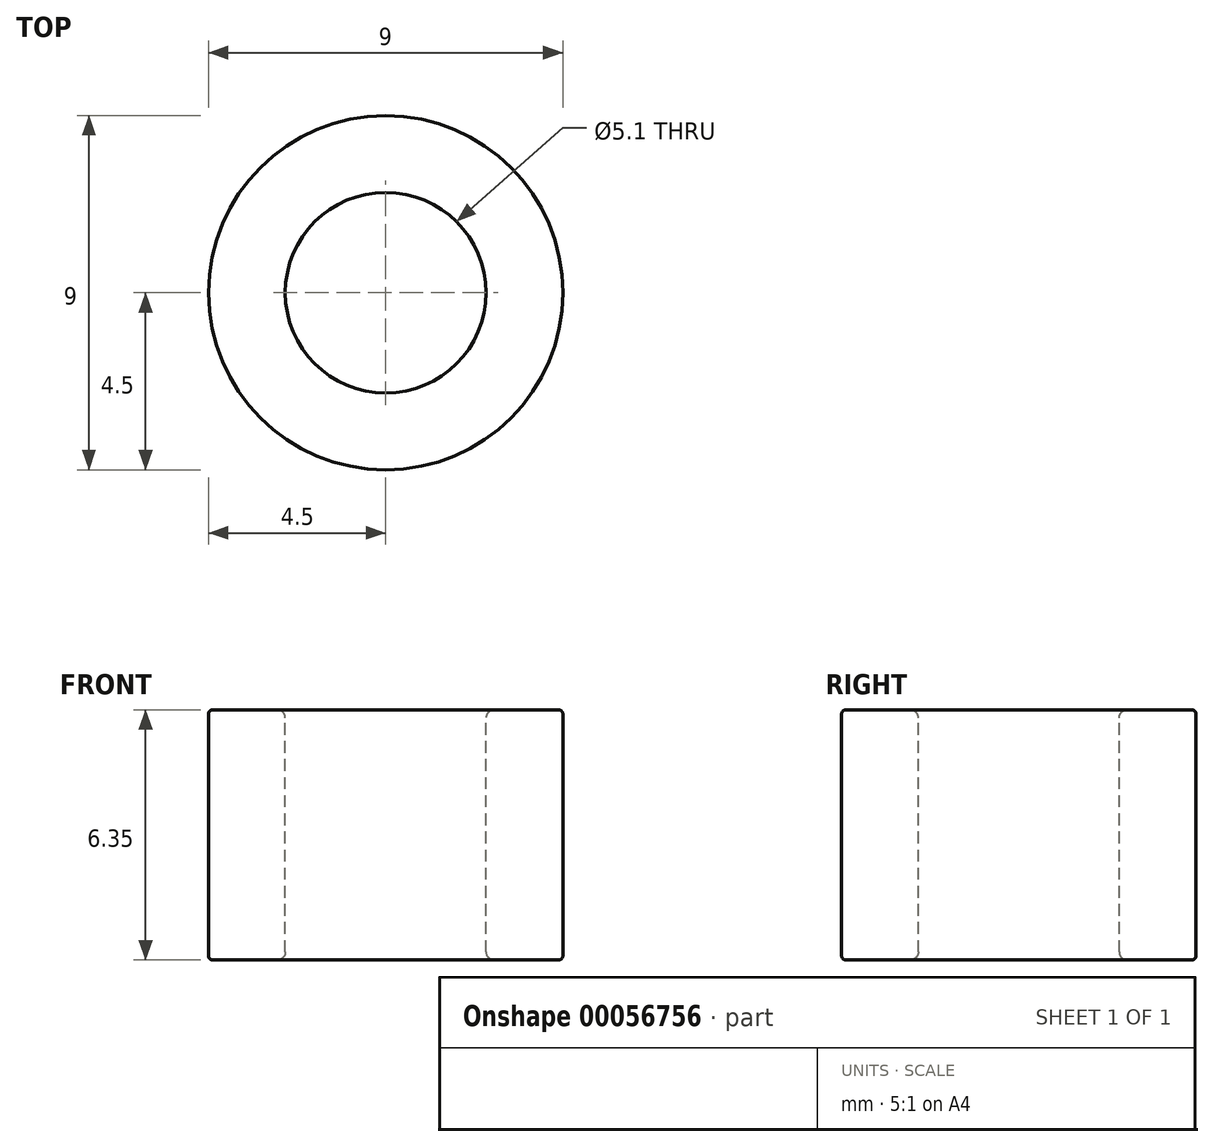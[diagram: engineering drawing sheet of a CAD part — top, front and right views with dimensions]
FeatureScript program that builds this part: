
annotation { "Feature Type Name" : "Feature", "Feature Type Description" : "" }
export const myFeature = defineFeature(function(context is Context, id is Id, definition is map)
    precondition{}
    {
        {
            var Q0;
            Q0=qCreatedBy(makeId("Front.planeOp"),FACE);
            var sketch = newSketch(context, id + "F0", { "sketchPlane" : qUnion([Q0])});
            skLineSegment(sketch, "E0", {"start": v(0, 5.54) * mm, "end": v(0, -7.32) * mm, "construction": true});
            skLineSegment(sketch, "E1", {"start": v(-2.75, 6.35) * mm, "end": v(-4.4, 6.35) * mm});
            skLineSegment(sketch, "E2", {"start": v(-4.5, 6.25) * mm, "end": v(-4.5, 0.1) * mm});
            skLineSegment(sketch, "E3", {"start": v(-4.4, 0) * mm, "end": v(-2.75, 0) * mm});
            skLineSegment(sketch, "E4", {"start": v(-2.55, 0.2) * mm, "end": v(-2.55, 6.15) * mm});
            skPoint(sketch, "E5.visualSharp", {"position": v(-4.5, 6.35) * mm});
            skArc(sketch, "E5.filletArc", {"start": v(-4.4, 6.35) * mm, "mid": v(-4.47, 6.32) * mm, "end": v(-4.5, 6.25) * mm});
            skPoint(sketch, "E6.visualSharp", {"position": v(-2.55, 6.35) * mm});
            skArc(sketch, "E6.filletArc", {"start": v(-2.55, 6.15) * mm, "mid": v(-2.6, 6.3) * mm, "end": v(-2.75, 6.35) * mm});
            skPoint(sketch, "E7.visualSharp", {"position": v(-4.5, 0) * mm});
            skArc(sketch, "E7.filletArc", {"start": v(-4.5, 0.1) * mm, "mid": v(-4.47, 0.03) * mm, "end": v(-4.4, 0) * mm});
            skPoint(sketch, "E8.visualSharp", {"position": v(-2.55, 0) * mm});
            skArc(sketch, "E8.filletArc", {"start": v(-2.75, 0) * mm, "mid": v(-2.6, 0.06) * mm, "end": v(-2.55, 0.2) * mm});
            skSolve(sketch);
        }
        {
            var Q0;
            Q0=qSketchRegion(id+"F0",true);
            var Q1;
            Q1=sQuery(id+"F0.wireOp",EDGE,"E0");
            revolve(context, id + "F1", {"entities" : qUnion([Q0]), "axis" : qUnion([Q1]), "revolveType" : RevolveType.FULL});
        }
    });
